# Revit family: FT Farm LED_2020
name_source: partatom
category: Lighting Fixtures
units: mm (PartAtom-declared; Revit-internal decimal feet)

## family parameters
Always vertical = Yes
Cut with Voids When Loaded = No
Light Source = Yes
OmniClass Number = 23.80.70.00
OmniClass Title = Lighting
Part Type = Normal
Room Calculation Point = No
Round Connector Dimension = Use Diameter
Shared = No
Work Plane-Based = No

## types (12) — shared parameters
Chromatic Index = CR>80
Color Filter = 16777215
Description = https://www.airfal.com
Dimming Lamp Color Temperature Shift = <None>
Emergency system = No
Emit from Line Length = 609.6 mm  [stored 2 ft]
IK = IK10
IP = IP69K
Led Module = Yes
MacAdam Ellipse = 3/4
Photobiological risk group = RG 0/1
URL = https://www.airfal.com
Unify glade rating = UGR<19
Useful life = L70B50>50000
zero-valued in all types: Default Elevation

## per-type parameters (varying)
| type | L | Net output | Photometric Web File | Size | Tilt Angle | Watts |
| Q0795 | 763 mm | 1155 lm | generic | 600 mm | 60.00° | 13 W |
| Q0899 | 763 mm | 1201 lm | generic | 600 mm | 60.00° | 13 W |
| Q0900 | 763 mm | 1984 lm | Q0900 FARM 600 16W 2650 lm G5.IES | 600 mm | 90.00° | 16 W |
| Q0955 | 763 mm | 2070 lm | Q0955 FARM 600 16W  2775 lm G5.IES | 600 mm | 90.00° | 16 W |
| Q0796 | 1375 mm  [stored 4.51115 ft] | 2310 lm | generic | 1200 mm | 60.00° | 24 W |
| Q0957 | 1375 mm  [stored 4.51115 ft] | 2480 lm | generic | 1200 mm | 60.00° | 24 W |
| Q0958 | 1375 mm  [stored 4.51115 ft] | 3969 lm | Q0958 FARM 1200 32W  5300 lm G5.IES | 1200 mm | 90.00° | 32 W |
| Q0959 | 1375 mm  [stored 4.51115 ft] | 4139 lm | Q0959 FARM 1200 32W 5550 lm G5.IES | 1200 mm | 90.00° | 32 W |
| Q0797 | 1660 mm  [stored 5.44619 ft] | 2883 lm | generic | 1500 mm  [stored 4.92126 ft] | 60.00° | 32 W |
| Q0961 | 1660 mm  [stored 5.44619 ft] | 3100 lm | generic | 1500 mm  [stored 4.92126 ft] | 60.00° | 29 W |
| Q0962 | 1660 mm  [stored 5.44619 ft] | 5193 lm | Q0962 FARM 1500 40W 6631 lm G5.IES | 1500 mm  [stored 4.92126 ft] | 90.00° | 40 W |
| Q0963 | 1660 mm  [stored 5.44619 ft] | 5193 lm | Q0963 FARM 1500 40W 6940 lm G5.IES | 1500 mm  [stored 4.92126 ft] | 90.00° | 40 W |

note: [stored X ft] marks values corroborated as IEEE doubles in the binary element streams (Revit-internal decimal feet)

## geometry (parser evidence)
native form markers: Blend x8, Sweep x18
no freeform markers — native parametric forms only
